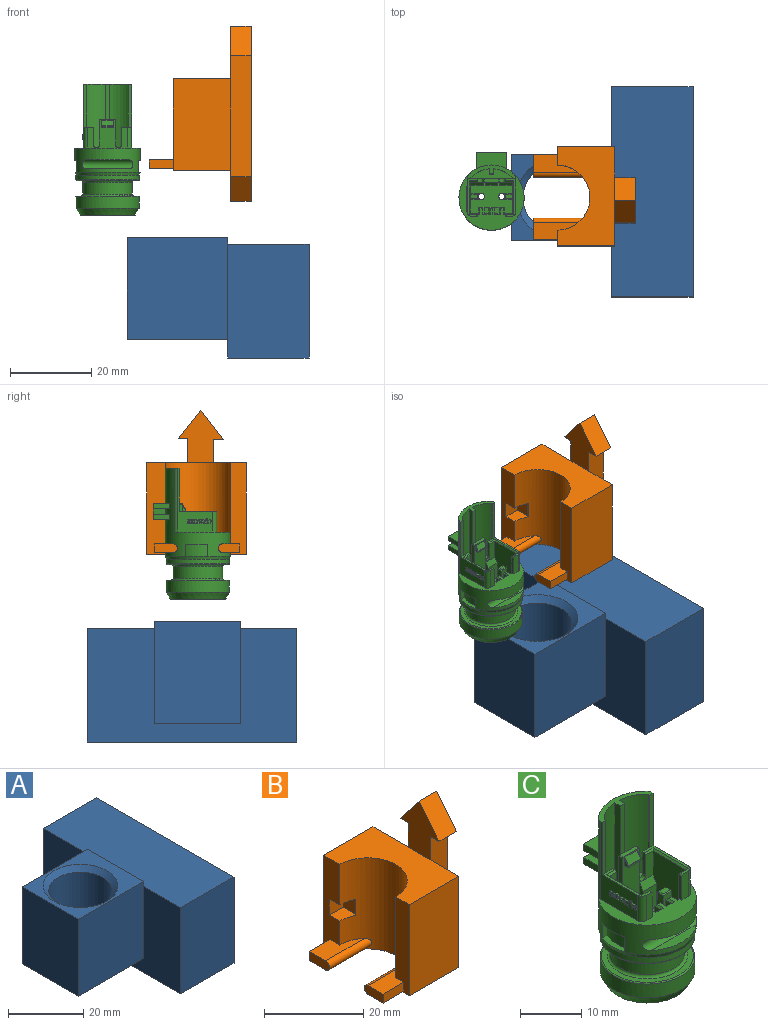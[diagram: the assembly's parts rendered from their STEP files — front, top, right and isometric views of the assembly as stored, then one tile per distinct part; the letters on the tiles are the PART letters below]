
ASSEMBLY  parts=3 mates=2
PART A: 14 faces, bbox 44.6x51.6x29.6 mm
  f0: plane 25x24.62mm, normal (0,1,0), area 615.4mm2, adj f1,f3,f5,f6,f13
  f1: plane 21.06x1.59mm, normal (1,0,0), area 33.5mm2, adj f0,f2,f6,f8
  f2: plane 25x24.62mm, normal (0,-1,0), area 615.4mm2, adj f1,f3,f5,f6,f13
  f3: plane 25x21.06mm, normal (-1,0,0), area 526.5mm2, adj f0,f2,f5,f6
  f4: cylinder r=8.43mm len=23.5mm, axis (0,0,1), area 1244.6mm2, adj f5,f7
  f5: plane 24.62x21.06mm, normal (0,0,-1), area 295.2mm2, adj f0,f2,f3,f4,f13
  f6: plane 24.62x21.06mm, normal (0,0,1), area 208.7mm2, adj f0,f1,f2,f3,f7
  f7: cone r=9.93mm half-angle=45deg, axis (0,0,1), area 122.3mm2, adj f4,f6
  f8: plane 51.57x20mm, normal (0,0,1), area 1031.3mm2, adj f1,f9,f11,f12,f13
  f9: plane 27.98x20mm, normal (0,-1,0), area 559.7mm2, adj f8,f10,f12,f13
  f10: plane 51.57x20mm, normal (0,0,-1), area 1031.3mm2, adj f9,f11,f12,f13
  f11: plane 27.98x20mm, normal (0,1,0), area 559.7mm2, adj f8,f10,f12,f13
  f12: plane 51.57x27.98mm, normal (1,0,0), area 1443.1mm2, adj f8,f9,f10,f11
  f13: plane 51.57x27.98mm, normal (-1,0,0), area 950mm2, adj f0,f2,f5,f8,f9,f10,f11
PART B: 37 faces, bbox 25x24.4x43.1 mm
  f0: plane 22.5x10.03mm, normal (1,0,0), area 225.7mm2, adj f4,f7,f8,f25
  f1: plane 22.5x8.17mm, normal (1,0,0), area 183.8mm2, adj f5,f7,f8,f30
  f2: cylinder r=8mm len=22.5mm, axis (0,0,-1), area 519.7mm2, adj f3,f6,f7,f8,f9,f10,f11,f14
  f3: plane 22.5x4.55mm, normal (-1,0,0), area 84.4mm2, adj f2,f4,f7,f8,f10,f11,f12,f19
  f4: plane 22.5x14.09mm, normal (0,1,0), area 317mm2, adj f0,f3,f7,f8
  f5: plane 22.5x14.09mm, normal (0,-1,0), area 317mm2, adj f1,f6,f7,f8
  f6: plane 22.5x3.9mm, normal (-1,0,0), area 82.6mm2, adj f2,f5,f7,f8,f15,f16,f17
  f7: plane 24.45x14.09mm, normal (0,0,1), area 243.9mm2, adj f0,f1,f2,f3,f4,f5,f6,f24
  f8: plane 24.45x14.09mm, normal (0,0,-1), area 243.9mm2, adj f0,f1,f2,f3,f4,f5,f6,f36
  f9: cylinder r=1.1mm len=12.16mm, axis (1,0,0), area 40.8mm2, adj f2,f10,f11,f13
  f10: plane 11.09x4.62mm, normal (0,0,-1), area 34.1mm2, adj f2,f3,f9,f12,f13
  f11: plane 11.09x4.62mm, normal (0,0,1), area 34.1mm2, adj f2,f3,f9,f12,f13
  f12: plane 5.91x2.2mm, normal (0,1,0), area 13mm2, adj f3,f10,f11,f13
  f13: plane 5.72x2.2mm, normal (-1,0,0), area 12.1mm2, adj f9,f10,f11,f12
  f14: cylinder r=1.1mm len=12.16mm, axis (1,0,0), area 40.8mm2, adj f2,f15,f17,f18
  f15: plane 11.09x4.21mm, normal (0,0,1), area 31.6mm2, adj f2,f6,f14,f16,f18
  f16: plane 5.91x2.2mm, normal (0,-1,0), area 13mm2, adj f6,f15,f17,f18
  f17: plane 11.09x4.21mm, normal (0,0,-1), area 31.6mm2, adj f2,f6,f14,f16,f18
  f18: plane 5.31x2.2mm, normal (-1,0,0), area 11.2mm2, adj f14,f15,f16,f17
  f19: plane 4x3.93mm, normal (0,0,-1), area 13.4mm2, adj f2,f3,f21,f22,f23
  f20: plane 4x3.93mm, normal (0,0,1), area 13.4mm2, adj f2,f3,f21,f22,f23
  f21: plane 4x0.25mm, normal (0,1,0), area 1mm2, adj f2,f19,f20,f23
  f22: plane 4x4mm, normal (0,-1,0), area 16mm2, adj f3,f19,f20,f23
  f23: plane 4x3.93mm, normal (-1,0,0), area 15.7mm2, adj f19,f20,f21,f22
  f24: plane 12.97x11.08mm, normal (-1,0,0), area 76mm2, adj f7,f25,f26,f27,f28,f29,f30
  f25: plane 30.16x5mm, normal (0,1,0), area 150.8mm2, adj f0,f24,f26,f34,f35,f36
  f26: plane 5x2.3mm, normal (0,0,-1), area 11.5mm2, adj f24,f25,f27,f35
  f27: plane 6.95x5.52mm, normal (0,0.78,0.62), area 44.4mm2, adj f24,f26,f28,f35
  f28: plane 7.2x5.56mm, normal (0,-0.79,0.61), area 45.5mm2, adj f24,f27,f29,f35
  f29: plane 5x2.53mm, normal (0,0,-1), area 12.7mm2, adj f24,f28,f30,f35
  f30: plane 29.78x5mm, normal (0,-1,0), area 148.9mm2, adj f1,f24,f29,f31,f35,f36
  f31: plane 5x2.53mm, normal (0,0,1), area 12.7mm2, adj f30,f32,f35,f36
  f32: plane 6.08x5.56mm, normal (0,-0.74,-0.67), area 41.2mm2, adj f31,f33,f35,f36
  f33: plane 5.94x5.52mm, normal (0,0.73,-0.68), area 40.5mm2, adj f32,f34,f35,f36
  f34: plane 5x2.3mm, normal (0,0,1), area 11.5mm2, adj f25,f33,f35,f36
  f35: plane 43.06x11.08mm, normal (1,0,0), area 259.9mm2, adj f25,f26,f27,f28,f29,f30,f31,f32
  f36: plane 11.08x7.59mm, normal (-1,0,0), area 43.2mm2, adj f8,f25,f30,f31,f32,f33,f34
PART C: 246 faces, bbox 16.8x19.4x32.2 mm
  f0: plane 0.81x0.16mm, normal (-1,0,0), area 0.1mm2, adj f1,f2,f3,f4
  f1: cylinder r=0.16mm len=0.25mm, axis (-1,0,0), area 0.1mm2, adj f0,f2,f4,f5
  f2: plane 0.81x0.25mm, normal (0,0,-1), area 0.2mm2, adj f0,f1,f3,f5
  f3: plane 0.25x0.16mm, normal (0,-1,0), area 0mm2, adj f0,f2,f4,f5
  f4: plane 0.65x0.25mm, normal (0,0,1), area 0.2mm2, adj f0,f1,f3,f5
  f5: plane 2.13x0.9mm, normal (-1,0,0), area 1.3mm2, adj f1,f2,f3,f4,f6,f7,f8,f9
  f6: plane 0.84x0.25mm, normal (0,0,-1), area 0.2mm2, adj f5,f7,f19,f24
  f7: cylinder r=0.54mm len=0.54mm, axis (-1,0,0), area 0.2mm2, adj f5,f6,f8,f24
  f8: plane 0.25x0.12mm, normal (0,0,1), area 0mm2, adj f5,f7,f9,f24
  f9: cylinder r=0.16mm len=0.25mm, axis (-1,0,0), area 0mm2, adj f5,f8,f10,f24
  f10: plane 0.25x0.19mm, normal (0,0,-1), area 0mm2, adj f5,f9,f11,f24
  f11: plane 0.41x0.25mm, normal (0,1,0), area 0.1mm2, adj f5,f10,f12,f24
  f12: cylinder r=0.25mm len=0.25mm, axis (-1,0,0), area 0.1mm2, adj f5,f11,f13,f24
  f13: plane 0.38x0.25mm, normal (0,0,-1), area 0.1mm2, adj f5,f12,f14,f24
  f14: plane 0.25x0.13mm, normal (0,-1,0), area 0mm2, adj f5,f13,f15,f24
  f15: plane 0.25x0.19mm, normal (0,0,1), area 0mm2, adj f5,f14,f16,f24
  f16: cylinder r=0.12mm len=0.25mm, axis (-1,0,0), area 0mm2, adj f5,f15,f17,f24
  f17: plane 0.65x0.25mm, normal (0,-1,0), area 0.2mm2, adj f5,f16,f18,f24
  f18: plane 1.82x0.25mm, normal (0,0,1), area 0.5mm2, adj f5,f17,f19,f24
  f19: plane 0.9x0.25mm, normal (0,1,0), area 0.2mm2, adj f5,f6,f18,f24
  f20: plane 0.25x0.12mm, normal (0,-1,0), area 0mm2, adj f5,f21,f23,f25
  f21: plane 0.8x0.25mm, normal (0,0,-1), area 0.2mm2, adj f5,f20,f22,f25
  f22: cylinder r=0.12mm len=0.25mm, axis (-1,0,0), area 0mm2, adj f5,f21,f23,f25
  f23: plane 0.68x0.25mm, normal (0,0,1), area 0.2mm2, adj f5,f20,f22,f25
  f24: plane 15.61x8.6mm, normal (-1,0,0), area 44.1mm2, adj f6,f7,f8,f9,f10,f11,f12,f13
  f25: plane 0.8x0.12mm, normal (-1,0,0), area 0.1mm2, adj f20,f21,f22,f23
  f26: cylinder r=1mm len=5.1mm, axis (0,0,-1), area 8mm2, adj f24,f27,f31,f81
  f27: plane 9.2x2.5mm, normal (0,0,1), area 6.3mm2, adj f24,f26,f28,f81,f82,f83,f84,f85
  f28: plane 10.51x0.8mm, normal (0,-1,0), area 8.4mm2, adj f24,f27,f29,f88
  f29: plane 11.8x3.4mm, normal (0,0,1), area 13.3mm2, adj f24,f28,f30,f88,f89,f90,f91,f92
  f30: cylinder r=1mm len=15.61mm, axis (0,0,-1), area 12.4mm2, adj f24,f29,f31,f89
  f31: plane 16x13.71mm, normal (0,0,1), area 68.6mm2, adj f24,f26,f30,f81,f89,f97,f98,f99
  f32: plane 0.33x0.25mm, normal (0,0,-1), area 0.1mm2, adj f24,f33,f35,f116
  f33: plane 0.25x0.12mm, normal (0,1,0), area 0mm2, adj f24,f32,f34,f116
  f34: plane 0.33x0.25mm, normal (0,0,1), area 0.1mm2, adj f24,f33,f35,f116
  f35: plane 0.25x0.12mm, normal (0,-1,0), area 0mm2, adj f24,f32,f34,f116
  f36: plane 0.25x0.2mm, normal (0,1,0), area 0mm2, adj f24,f37,f54,f117
  f37: plane 1.82x0.25mm, normal (0,0,1), area 0.5mm2, adj f24,f36,f38,f117
  f38: cylinder r=0.55mm len=0.46mm, axis (-1,0,0), area 0.1mm2, adj f24,f37,f39,f117
  f39: cylinder r=0.27mm len=0.25mm, axis (-1,0,0), area 0.1mm2, adj f24,f38,f40,f117
  f40: plane 0.25x0.2mm, normal (0,-1,0), area 0mm2, adj f24,f39,f41,f117
  f41: plane 0.25x0.09mm, normal (0,0,-1), area 0mm2, adj f24,f40,f42,f117
  f42: plane 0.25x0.2mm, normal (0,1,0), area 0mm2, adj f24,f41,f43,f117
  f43: cylinder r=0.19mm len=0.25mm, axis (-1,0,0), area 0.1mm2, adj f24,f42,f44,f117
  f44: plane 0.37x0.25mm, normal (0,0,-1), area 0.1mm2, adj f24,f43,f45,f117
  f45: plane 0.38x0.25mm, normal (0,-1,0), area 0.1mm2, adj f24,f44,f46,f117
  f46: plane 0.32x0.25mm, normal (0,0,-1), area 0.1mm2, adj f24,f45,f47,f117
  f47: plane 0.54x0.25mm, normal (0,1,0), area 0.1mm2, adj f24,f46,f48,f117
  f48: plane 0.65x0.25mm, normal (0,0,1), area 0.2mm2, adj f24,f47,f49,f117
  f49: cylinder r=0.16mm len=0.25mm, axis (-1,0,0), area 0.1mm2, adj f24,f48,f50,f117
  f50: plane 0.92x0.25mm, normal (0,0,-1), area 0.2mm2, adj f24,f49,f51,f117
  f51: plane 0.7x0.25mm, normal (0,-1,0), area 0.2mm2, adj f24,f50,f52,f117
  f52: plane 0.29x0.25mm, normal (0,0,-1), area 0.1mm2, adj f24,f51,f53,f117
  f53: plane 0.7x0.25mm, normal (0,1,0), area 0.2mm2, adj f24,f52,f54,f117
  f54: plane 0.33x0.25mm, normal (0,0,-1), area 0.1mm2, adj f24,f36,f53,f117
  f55: plane 0.51x0.25mm, normal (0,1,0), area 0.1mm2, adj f24,f56,f70,f118
  f56: plane 0.56x0.25mm, normal (0,0,1), area 0.1mm2, adj f24,f55,f57,f118
  f57: plane 0.53x0.3mm, normal (0,-0.87,-0.49), area 0.2mm2, adj f24,f56,f58,f118
  f58: plane 0.81x0.56mm, normal (0,0.82,0.57), area 0.2mm2, adj f24,f57,f59,f118
  f59: plane 0.81x0.46mm, normal (0,-0.87,-0.49), area 0.2mm2, adj f24,f58,f60,f118
  f60: plane 0.81x0.56mm, normal (0,0.82,0.57), area 0.2mm2, adj f24,f59,f61,f118
  f61: plane 0.78x0.44mm, normal (0,-0.87,-0.49), area 0.2mm2, adj f24,f60,f62,f118
  f62: plane 0.81x0.56mm, normal (0,0.82,0.57), area 0.2mm2, adj f24,f61,f63,f118
  f63: plane 0.78x0.44mm, normal (0,-0.87,-0.49), area 0.2mm2, adj f24,f62,f64,f118
  f64: plane 0.81x0.56mm, normal (0,0.82,0.57), area 0.2mm2, adj f24,f63,f65,f118
  f65: plane 0.81x0.46mm, normal (0,-0.87,-0.49), area 0.2mm2, adj f24,f64,f66,f118
  f66: plane 0.42x0.29mm, normal (0,0.82,0.57), area 0.1mm2, adj f24,f65,f67,f118
  f67: cylinder r=0.38mm len=0.34mm, axis (-1,0,0), area 0.1mm2, adj f24,f66,f68,f118
  f68: plane 0.51x0.25mm, normal (0,-1,0), area 0.1mm2, adj f24,f67,f69,f118
  f69: plane 0.81x0.25mm, normal (0,0,-1), area 0.2mm2, adj f24,f68,f70,f118
  f70: cylinder r=0.38mm len=0.38mm, axis (-1,0,0), area 0.2mm2, adj f24,f55,f69,f118
  f71: plane 0.25x0.2mm, normal (0,0,-1), area 0mm2, adj f24,f72,f80,f119
  f72: plane 0.9x0.25mm, normal (0,1,0), area 0.2mm2, adj f24,f71,f73,f119
  f73: plane 0.67x0.25mm, normal (0,0,1), area 0.2mm2, adj f24,f72,f74,f119
  f74: cylinder r=0.36mm len=0.36mm, axis (-1,0,0), area 0.1mm2, adj f24,f73,f75,f119
  f75: plane 0.54x0.25mm, normal (0,-1,0), area 0.1mm2, adj f24,f74,f76,f119
  f76: plane 0.28x0.25mm, normal (0,0,-1), area 0.1mm2, adj f24,f75,f77,f119
  f77: plane 0.54x0.25mm, normal (0,1,0), area 0.1mm2, adj f24,f76,f78,f119
  f78: cylinder r=0.15mm len=0.25mm, axis (-1,0,0), area 0.1mm2, adj f24,f77,f79,f119
  f79: plane 0.4x0.25mm, normal (0,0,-1), area 0.1mm2, adj f24,f78,f80,f119
  f80: plane 0.68x0.25mm, normal (0,-1,0), area 0.2mm2, adj f24,f71,f79,f119
  f81: plane 5.1x1.55mm, normal (0,-1,0), area 7.9mm2, adj f26,f27,f31,f87,f99
  f82: plane 5.1x2.4mm, normal (0,1,0), area 8.8mm2, adj f27,f83,f88,f120,f121
  f83: plane 4.4x0.8mm, normal (1,0,0), area 3.5mm2, adj f27,f82,f84,f120,f122
  f84: plane 2x0.3mm, normal (0,-0.71,0.71), area 0.8mm2, adj f27,f83,f85,f122
  f85: plane 8.2x0.3mm, normal (0.71,0,0.71), area 3.4mm2, adj f27,f84,f86,f123
  f86: plane 2.05x0.3mm, normal (0,0.71,0.71), area 0.7mm2, adj f27,f85,f87,f124
  f87: plane 0.8x0.3mm, normal (0.71,0,0.71), area 0.3mm2, adj f27,f81,f86,f99
  f88: plane 15.61x0.34mm, normal (1,0,0), area 5.3mm2, adj f28,f29,f82,f90,f121
  f89: cylinder r=8mm len=21.61mm, axis (0,0,1), area 379.5mm2, adj f29,f30,f31,f98,f125,f126,f127,f128
  f90: cylinder r=7.1mm len=15.61mm, axis (0,0,1), area 81mm2, adj f29,f88,f91,f121
  f91: plane 15.61x1.28mm, normal (-1,0,0), area 20mm2, adj f29,f90,f92,f121
  f92: plane 15.61x1mm, normal (0,-1,0), area 15.6mm2, adj f29,f91,f93,f121
  f93: plane 15.61x1.28mm, normal (1,0,0), area 20mm2, adj f29,f92,f94,f121
  f94: cylinder r=7.1mm len=15.61mm, axis (0,0,1), area 81mm2, adj f29,f93,f95,f121
  f95: plane 15.61x0.34mm, normal (-1,0,0), area 5.3mm2, adj f29,f94,f96,f121,f148
  f96: plane 10.51x0.8mm, normal (0,-1,0), area 8.4mm2, adj f29,f95,f97,f149
  f97: plane 15.61x8.6mm, normal (1,0,0), area 48.1mm2, adj f29,f31,f96,f98,f115,f149
  f98: cylinder r=1mm len=15.61mm, axis (0,0,-1), area 12.4mm2, adj f29,f31,f89,f97
  f99: plane 5.1x0.8mm, normal (1,0,0), area 3.9mm2, adj f31,f81,f87,f100,f124
  f100: plane 0.5x0.3mm, normal (0,0.71,0.71), area 0.1mm2, adj f31,f99,f101,f124
  f101: plane 1.7x0.3mm, normal (-0.71,0,0.71), area 0.6mm2, adj f31,f100,f102,f153
  f102: plane 1.3x0.3mm, normal (0,0.71,0.71), area 0.4mm2, adj f31,f101,f103,f154
  f103: plane 1.7x0.3mm, normal (0.71,0,0.71), area 0.6mm2, adj f31,f102,f104,f155
  f104: plane 1.8x0.3mm, normal (0,0.71,0.71), area 0.6mm2, adj f31,f103,f105,f156
  f105: plane 1.7x0.3mm, normal (-0.71,0,0.71), area 0.6mm2, adj f31,f104,f106,f157
  f106: plane 1.3x0.3mm, normal (0,0.71,0.71), area 0.4mm2, adj f31,f105,f107,f158
  f107: plane 1.7x0.3mm, normal (0.71,0,0.71), area 0.6mm2, adj f31,f106,f108,f159
  f108: plane 1.8x0.3mm, normal (0,0.71,0.71), area 0.6mm2, adj f31,f107,f109,f160
  f109: plane 1.7x0.3mm, normal (-0.71,0,0.71), area 0.6mm2, adj f31,f108,f110,f161
  f110: plane 1.3x0.3mm, normal (0,0.71,0.71), area 0.4mm2, adj f31,f109,f111,f162
  f111: plane 1.7x0.3mm, normal (0.71,0,0.71), area 0.6mm2, adj f31,f110,f112,f163
  f112: plane 0.5x0.3mm, normal (0,0.71,0.71), area 0.1mm2, adj f31,f111,f113,f164
  f113: plane 5.1x0.8mm, normal (-1,0,0), area 3.9mm2, adj f31,f112,f114,f164,f165
  f114: plane 5.1x1.55mm, normal (0,-1,0), area 7.9mm2, adj f31,f113,f115,f149,f165
  f115: cylinder r=1mm len=5.1mm, axis (0,0,-1), area 8mm2, adj f31,f97,f114,f149
  f116: plane 0.33x0.12mm, normal (-1,0,0), area 0mm2, adj f32,f33,f34,f35
  f117: plane 1.82x0.9mm, normal (-1,0,0), area 0.9mm2, adj f36,f37,f38,f39,f40,f41,f42,f43
  f118: plane 1.25x1.2mm, normal (-1,0,0), area 1mm2, adj f55,f56,f57,f58,f59,f60,f61,f62
  f119: plane 1.03x0.9mm, normal (-1,0,0), area 0.5mm2, adj f71,f72,f73,f74,f75,f76,f77,f78
  f120: cylinder r=0.7mm len=1.4mm, axis (0,-1,0), area 1.8mm2, adj f82,f83,f122,f166,f167,f168
  f121: plane 10.2x2.48mm, normal (0,0,1), area 17.4mm2, adj f82,f88,f90,f91,f92,f93,f94,f95
  f122: plane 4.8x2.4mm, normal (0,-1,0), area 8.3mm2, adj f83,f84,f120,f123,f169
  f123: plane 10.8x7.6mm, normal (1,0,0), area 70.9mm2, adj f85,f122,f124,f169,f170,f171,f172,f173
  f124: plane 10.8x1.95mm, normal (0,1,0), area 20mm2, adj f86,f99,f100,f123,f153,f170
  f125: plane 10.35x1.9mm, normal (0,0,-1), area 13.5mm2, adj f89,f126
  f126: cylinder r=1.1mm len=12.49mm, axis (1,0,0), area 39.5mm2, adj f89,f125,f127
  f127: plane 10.35x1.9mm, normal (0,0,1), area 13.5mm2, adj f89,f126
  f128: cone r=7.88mm half-angle=20deg, axis (0,0,1), area 0mm2, adj f89,f129,f130
  f129: cone r=7.88mm half-angle=20deg, axis (0,0,1), area 36.1mm2, adj f89,f128,f132,f150,f152,f177,f178,f186
  f130: plane 3x1.06mm, normal (0,1,0), area 3.2mm2, adj f89,f128,f131,f178,f179
  f131: plane 5.4x1.68mm, normal (0,0,-1), area 5.5mm2, adj f89,f130,f132,f179
  f132: plane 3x1.09mm, normal (0,-1,0), area 3.3mm2, adj f89,f129,f131,f178,f179
  f133: plane 10.35x1.9mm, normal (0,0,1), area 13.5mm2, adj f89,f134
  f134: cylinder r=1.1mm len=12.49mm, axis (1,0,0), area 39.5mm2, adj f89,f133,f135
  f135: plane 10.35x1.9mm, normal (0,0,-1), area 13.5mm2, adj f89,f134
  f136: plane 7.5x3.93mm, normal (0,0,-1), area 24.8mm2, adj f89,f137,f147,f180
  f137: plane 3.93x1.3mm, normal (1,0,0), area 5.1mm2, adj f89,f136,f138,f180
  f138: plane 3.93x3.1mm, normal (0,0,1), area 10.4mm2, adj f89,f137,f139,f180
  f139: plane 3.03x1.4mm, normal (1,0,0), area 4.2mm2, adj f89,f138,f140,f180
  f140: plane 3.93x3.1mm, normal (0,0,-1), area 10.4mm2, adj f89,f139,f141,f180
  f141: plane 3.93x1.3mm, normal (1,0,0), area 5.1mm2, adj f89,f140,f142,f180
  f142: plane 7.5x3.93mm, normal (0,0,1), area 24.8mm2, adj f89,f141,f143,f180
  f143: plane 3.93x1.3mm, normal (-1,0,0), area 5.1mm2, adj f89,f142,f144,f180
  f144: plane 3.93x3.1mm, normal (0,0,-1), area 10.4mm2, adj f89,f143,f145,f180
  f145: plane 3.03x1.4mm, normal (-1,0,0), area 4.2mm2, adj f89,f144,f146,f180
  f146: plane 3.93x3.1mm, normal (0,0,1), area 10.4mm2, adj f89,f145,f147,f180
  f147: plane 3.93x1.3mm, normal (-1,0,0), area 5.1mm2, adj f89,f136,f146,f180
  f148: plane 5.1x2.4mm, normal (0,1,0), area 8.8mm2, adj f95,f121,f149,f181,f182
  f149: plane 9.2x2.5mm, normal (0,0,1), area 6.3mm2, adj f96,f97,f114,f115,f148,f165,f182,f183
  f150: plane 3x1.09mm, normal (0,-1,0), area 3.3mm2, adj f89,f129,f151,f186,f187
  f151: plane 5.4x1.68mm, normal (0,0,-1), area 5.5mm2, adj f89,f150,f152,f187
  f152: plane 3x1.06mm, normal (0,1,0), area 3.2mm2, adj f89,f129,f151,f186,f187
  f153: plane 5.7x1.4mm, normal (-1,0,0), area 8mm2, adj f101,f124,f154,f170
  f154: plane 5.7x1.3mm, normal (0,1,0), area 7.4mm2, adj f102,f153,f155,f170
  f155: plane 10.2x1.4mm, normal (1,0,0), area 14.3mm2, adj f103,f154,f156,f188,f189
  f156: plane 10.2x1.2mm, normal (0,1,0), area 12.2mm2, adj f104,f155,f157,f188
  f157: plane 10.2x1.4mm, normal (-1,0,0), area 14.3mm2, adj f105,f156,f158,f188,f189
  f158: plane 5.7x1.3mm, normal (0,1,0), area 7.4mm2, adj f106,f157,f159,f170
  f159: plane 10.2x1.4mm, normal (1,0,0), area 14.3mm2, adj f107,f158,f160,f190,f191
  f160: plane 10.2x1.2mm, normal (0,1,0), area 12.2mm2, adj f108,f159,f161,f190
  f161: plane 10.2x1.4mm, normal (-1,0,0), area 14.3mm2, adj f109,f160,f162,f190,f191
  f162: plane 5.7x1.3mm, normal (0,1,0), area 7.4mm2, adj f110,f161,f163,f170
  f163: plane 5.7x1.4mm, normal (1,0,0), area 8mm2, adj f111,f162,f164,f170
  f164: plane 10.8x1.95mm, normal (0,1,0), area 20mm2, adj f112,f113,f163,f170,f185,f192
  f165: plane 0.8x0.3mm, normal (-0.71,0,0.71), area 0.3mm2, adj f113,f114,f149,f185
  f166: plane 7x5.4mm, normal (0,1,0), area 28.2mm2, adj f120,f121,f167,f181,f193,f194,f195,f196
  f167: plane 6.1x0.8mm, normal (-1,0,0), area 4.9mm2, adj f120,f166,f168,f193
  f168: plane 13.06x5.46mm, normal (0,-1,0), area 47.3mm2, adj f120,f167,f169,f170,f181,f193,f194,f195
  f169: plane 3.1x1.39mm, normal (0,-0.87,0.5), area 5mm2, adj f122,f123,f168,f176,f197
  f170: plane 10.2x7.6mm, normal (0,0,1), area 55mm2, adj f123,f124,f153,f154,f158,f162,f163,f164
  f171: plane 4.8x1.85mm, normal (0,-1,0), area 8.9mm2, adj f123,f170,f172,f207
  f172: plane 1.85x0.2mm, normal (0,-0.71,0.71), area 0.5mm2, adj f123,f171,f173,f211
  f173: plane 1.65x1mm, normal (0,0,1), area 1.7mm2, adj f123,f172,f174,f211
  f174: plane 1.85x0.2mm, normal (0,0.71,0.71), area 0.5mm2, adj f123,f173,f175,f211
  f175: plane 4.8x1.85mm, normal (0,1,0), area 8.9mm2, adj f123,f170,f174,f207
  f176: plane 4.61x3.1mm, normal (0,-1,0), area 14.3mm2, adj f123,f169,f170,f197
  f177: cylinder r=7.75mm len=15.5mm, axis (0,0,-1), area 54.5mm2, adj f129,f214
  f178: plane 5.4x1.67mm, normal (0,0,1), area 5.5mm2, adj f129,f130,f132,f179
  f179: cylinder r=7mm len=5.4mm, axis (0,0,1), area 16.7mm2, adj f130,f131,f132,f178
  f180: plane 7.5x4mm, normal (0,1,0), area 21.3mm2, adj f136,f137,f138,f139,f140,f141,f142,f143
  f181: cylinder r=0.7mm len=1.4mm, axis (0,-1,0), area 1.8mm2, adj f148,f166,f168,f182,f196,f215
  f182: plane 4.4x0.8mm, normal (-1,0,0), area 3.5mm2, adj f148,f149,f181,f184,f215
  f183: plane 8.2x0.3mm, normal (-0.71,0,0.71), area 3.4mm2, adj f149,f184,f185,f192
  f184: plane 2x0.3mm, normal (0,-0.71,0.71), area 0.8mm2, adj f149,f182,f183,f215
  f185: plane 2.05x0.3mm, normal (0,0.71,0.71), area 0.7mm2, adj f149,f164,f165,f183
  f186: plane 5.4x1.67mm, normal (0,0,1), area 5.5mm2, adj f129,f150,f152,f187
  f187: cylinder r=7mm len=5.4mm, axis (0,0,1), area 16.7mm2, adj f150,f151,f152,f186
  f188: plane 1.4x1.2mm, normal (0,0,1), area 1.7mm2, adj f155,f156,f157,f189
  f189: plane 4.5x1.2mm, normal (0,-1,0), area 5.4mm2, adj f155,f157,f170,f188
  f190: plane 1.4x1.2mm, normal (0,0,1), area 1.7mm2, adj f159,f160,f161,f191
  f191: plane 4.5x1.2mm, normal (0,-1,0), area 5.4mm2, adj f159,f161,f170,f190
  f192: plane 10.8x7.6mm, normal (-1,0,0), area 70.9mm2, adj f164,f170,f183,f198,f208,f212,f213,f215
  f193: cylinder r=0.2mm len=0.8mm, axis (0,-1,0), area 0.3mm2, adj f166,f167,f168,f194
  f194: plane 3.6x0.8mm, normal (0,0,1), area 2.9mm2, adj f166,f168,f193,f195
  f195: cylinder r=0.2mm len=0.8mm, axis (0,1,0), area 0.3mm2, adj f166,f168,f194,f196
  f196: plane 6.1x0.8mm, normal (1,0,0), area 4.9mm2, adj f166,f168,f181,f195
  f197: plane 6x0.8mm, normal (1,0,0), area 4.2mm2, adj f168,f169,f170,f176
  f198: plane 3.1x1.39mm, normal (0,-0.87,0.5), area 5mm2, adj f168,f192,f199,f213,f215
  f199: plane 6x0.8mm, normal (-1,0,0), area 4.2mm2, adj f168,f170,f198,f213
  f200: plane 2.8x1.36mm, normal (0,-0.87,0.5), area 4.4mm2, adj f168,f201,f205,f219
  f201: cylinder r=0.1mm len=1.41mm, axis (0,0.5,0.87), area 0.2mm2, adj f168,f200,f202,f220
  f202: plane 1.49x0.7mm, normal (-1,0,0), area 0.6mm2, adj f168,f201,f203,f221
  f203: plane 3x0.8mm, normal (0,0.09,-1), area 2.4mm2, adj f168,f202,f204,f221,f222,f223
  f204: plane 1.49x0.7mm, normal (1,0,0), area 0.6mm2, adj f168,f203,f205,f223
  f205: cylinder r=0.1mm len=1.41mm, axis (0,-0.5,-0.87), area 0.2mm2, adj f168,f200,f204,f224
  f206: cylinder r=0.75mm len=4.5mm, axis (0,0,1), area 21.2mm2, adj f170,f225
  f207: plane 4.8x1.4mm, normal (1,0,0), area 6.7mm2, adj f170,f171,f175,f211
  f208: plane 4.8x1.85mm, normal (0,-1,0), area 8.9mm2, adj f170,f192,f209,f218
  f209: plane 4.8x1.4mm, normal (-1,0,0), area 6.7mm2, adj f170,f208,f212,f226
  f210: cylinder r=0.75mm len=4.5mm, axis (0,0,1), area 21.2mm2, adj f170,f227
  f211: plane 1.4x0.2mm, normal (0.71,0,0.71), area 0.3mm2, adj f172,f173,f174,f207
  f212: plane 4.8x1.85mm, normal (0,1,0), area 8.9mm2, adj f170,f192,f209,f216
  f213: plane 4.61x3.1mm, normal (0,-1,0), area 14.3mm2, adj f170,f192,f198,f199
  f214: torus R=7.55mm, axis (0,0,-1), area 15.2mm2, adj f177,f228
  f215: plane 4.8x2.4mm, normal (0,-1,0), area 8.3mm2, adj f181,f182,f184,f192,f198
  f216: plane 1.85x0.2mm, normal (0,0.71,0.71), area 0.5mm2, adj f192,f212,f217,f226
  f217: plane 1.65x1mm, normal (0,0,1), area 1.7mm2, adj f192,f216,f218,f226
  f218: plane 1.85x0.2mm, normal (0,-0.71,0.71), area 0.5mm2, adj f192,f208,f217,f226
  f219: cylinder r=0.1mm len=2.8mm, axis (-1,0,0), area 0.1mm2, adj f200,f220,f222,f224
  f220: sphere r=0.1mm, area 0mm2, adj f201,f219,f221
  f221: cylinder r=0.1mm len=0.29mm, axis (0,0,-1), area 0mm2, adj f202,f203,f220,f222
  f222: plane 2.8x0.29mm, normal (0,-1,0), area 0.8mm2, adj f203,f219,f221,f223
  f223: cylinder r=0.1mm len=0.29mm, axis (0,0,1), area 0mm2, adj f203,f204,f222,f224
  f224: sphere r=0.1mm, area 0mm2, adj f205,f219,f223
  f225: cone r=0.93mm half-angle=10deg, axis (0,0,-1), area 11.8mm2, adj f206,f245
  f226: plane 1.4x0.2mm, normal (-0.71,0,0.71), area 0.3mm2, adj f209,f216,f217,f218
  f227: cone r=0.93mm half-angle=10deg, axis (0,0,-1), area 11.8mm2, adj f210,f245
  f228: plane 15.1x15.1mm, normal (0,0,-1), area 44.3mm2, adj f214,f229
  f229: torus R=6.55mm, axis (0,0,-1), area 30.8mm2, adj f228,f234
  f230: cylinder r=6mm len=12mm, axis (0,0,-1), area 101.6mm2, adj f231,f233,f235,f245
  f231: cylinder r=2mm len=3.5mm, axis (0,0,-1), area 5.1mm2, adj f230,f232,f236,f245
  f232: plane 5.29x3.5mm, normal (0,-1,0), area 18.5mm2, adj f231,f233,f237,f245
  f233: cylinder r=2mm len=3.5mm, axis (0,0,-1), area 5.1mm2, adj f230,f232,f238,f245
  f234: cylinder r=6.05mm len=12.1mm, axis (0,0,-1), area 106.4mm2, adj f229,f239
  f235: cone r=6.25mm half-angle=45deg, axis (0,0,-1), area 21.4mm2, adj f230,f236,f238,f240
  f236: cone r=2.25mm half-angle=45deg, axis (0,0,-1), area 1.1mm2, adj f231,f235,f237,f240
  f237: plane 5.29x0.5mm, normal (0,-0.71,-0.71), area 3.7mm2, adj f232,f236,f238,f240
  f238: cone r=2.25mm half-angle=45deg, axis (0,0,-1), area 1.1mm2, adj f233,f235,f237,f240
  f239: torus R=6.55mm, axis (0,0,-1), area 30.8mm2, adj f234,f241
  f240: plane 13.52x13.5mm, normal (0,0,-1), area 15.3mm2, adj f235,f236,f237,f238,f242
  f241: plane 15.1x15.1mm, normal (0,0,1), area 44.3mm2, adj f239,f243
  f242: cone r=7.25mm half-angle=30deg, axis (0,0,1), area 91.1mm2, adj f240,f244
  f243: torus R=7.55mm, axis (0,0,-1), area 15.2mm2, adj f241,f244
  f244: cylinder r=7.75mm len=15.5mm, axis (0,0,-1), area 134.8mm2, adj f242,f243
  f245: plane 12x11mm, normal (0,0,-1), area 100.9mm2, adj f225,f227,f230,f231,f232,f233
PLACE A at identity fixed
PLACE B t=(0,0,16.5)mm
PLACE C t=(-29.08,-4.82,15.15)mm
MATE slider B.f14 <-> C.f126  axis (1,0,0) through (-12.71,-10.92,19.15)mm
MATE slider A.f4 <-> B.f2  axis (0,0,1) through (-12.91,-4.82,-12.1)mm
